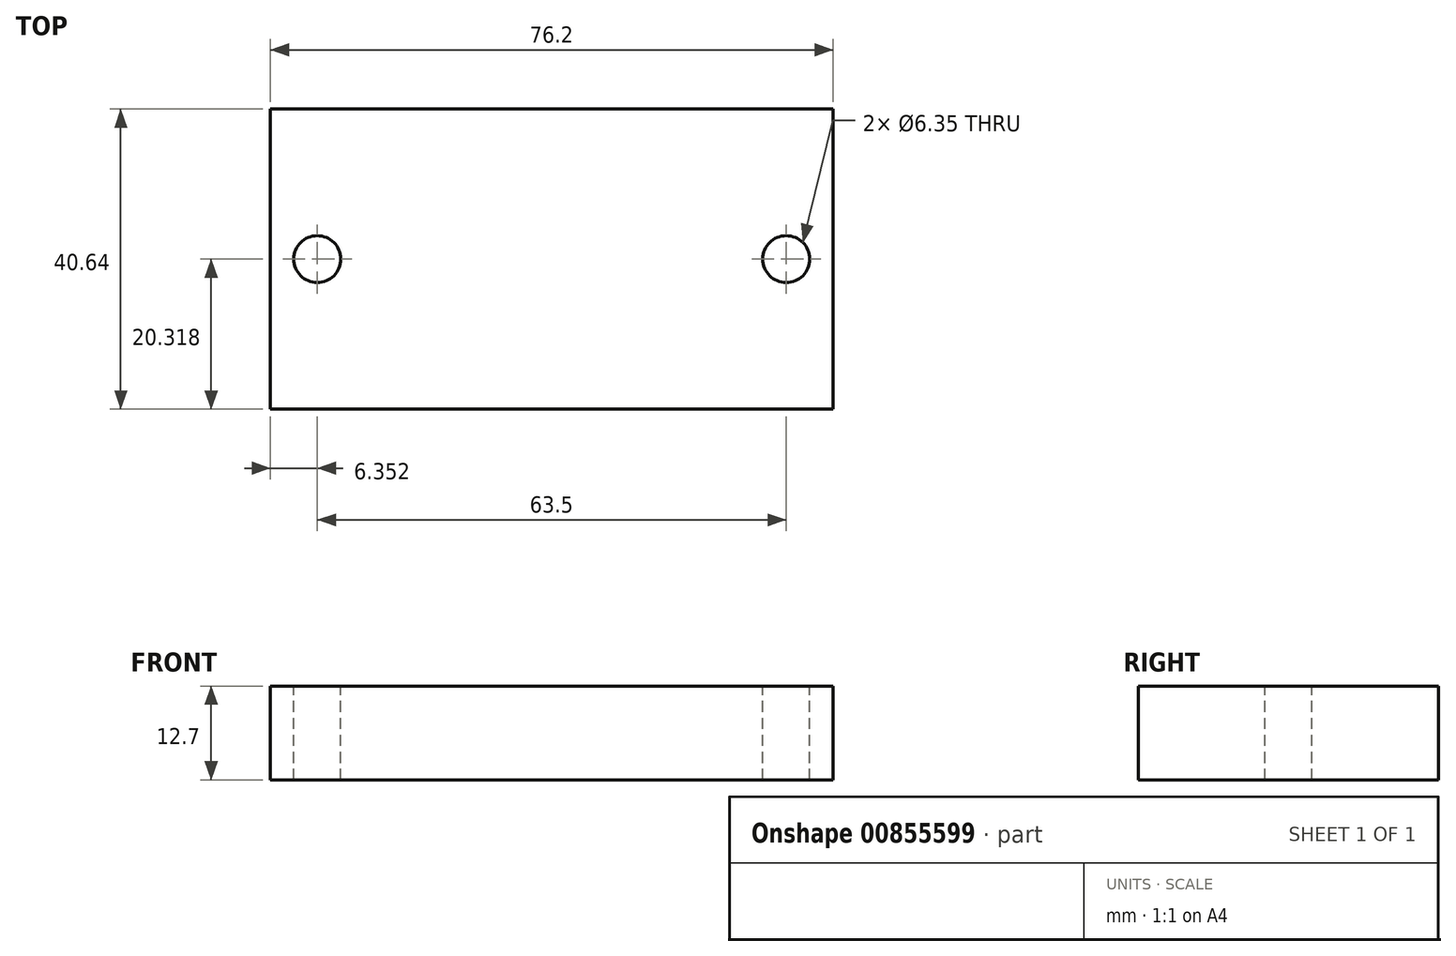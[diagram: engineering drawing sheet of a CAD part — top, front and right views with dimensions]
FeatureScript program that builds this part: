
annotation { "Feature Type Name" : "Feature", "Feature Type Description" : "" }
export const myFeature = defineFeature(function(context is Context, id is Id, definition is map)
    precondition{}
    {
        {
            var Q0;
            Q0=qCreatedBy(makeId("Top.planeOp"),FACE);
            var sketch = newSketch(context, id + "F0", { "sketchPlane" : qUnion([Q0])});
            skLineSegment(sketch, "E0.bottom", {"start": v(-33.33, 30.05) * mm, "end": v(42.87, 30.05) * mm});
            skLineSegment(sketch, "E0.top", {"start": v(-33.33, -10.6) * mm, "end": v(42.87, -10.6) * mm});
            skLineSegment(sketch, "E0.left", {"start": v(-33.33, 30.05) * mm, "end": v(-33.33, -10.6) * mm});
            skLineSegment(sketch, "E0.right", {"start": v(42.87, 30.05) * mm, "end": v(42.87, -10.6) * mm});
            skSolve(sketch);
        }
        {
            var Q0;
            Q0 = qSketchRegion(id + "F0", true);
            extrude(context, id + "F1", {"entities" : qUnion([Q0]), "depth" : 12.7 * mm, "offsetDistance" : 25.4 * mm});
        }
        {
            var Q0;
            Q0=makeQuery(id+"F1.opExtrude","CAP_FACE",FACE,{"disambiguationData":[OSD([sQuery(id+"F0.wireOp",EDGE,"E0.bottom"),sQuery(id+"F0.wireOp",EDGE,"E0.top"),sQuery(id+"F0.wireOp",EDGE,"E0.left"),sQuery(id+"F0.wireOp",EDGE,"E0.right")])],"isStart":false});
            var sketch = newSketch(context, id + "F2", { "sketchPlane" : qUnion([Q0])});
            skCircle(sketch, "E1", {"center": v(-26.98, 9.73) * mm, "radius": 3.18 * mm});
            skPoint(sketch, "E2", {"position": v(42.87, 9.73) * mm});
            skLineSegment(sketch, "E3", {"start": v(42.87, 9.73) * mm, "end": v(89.4, 9.73) * mm, "construction": true});
            skLineSegment(sketch, "E4", {"start": v(-26.98, 9.73) * mm, "end": v(-6.04, 9.73) * mm, "construction": true});
            skPoint(sketch, "E5", {"position": v(4.77, 30.05) * mm});
            skLineSegment(sketch, "E6", {"start": v(4.77, 30.05) * mm, "end": v(4.77, 48.42) * mm, "construction": true});
            skCircle(sketch, "E7.MirrorC", {"center": v(36.52, 9.73) * mm, "radius": 3.18 * mm});
            skSolve(sketch);
        }
        {
            var Q0;
            Q0 = qSketchRegion(id + "F2", true);
            extrude(context, id + "F3", {"entities" : qUnion([Q0]), "operationType" : NewBodyOperationType.REMOVE, "endBound" : BoundingType.UP_TO_NEXT, "oppositeDirection" : true, "depth" : 25.4 * mm, "offsetDistance" : 25.4 * mm});
        }
    });
